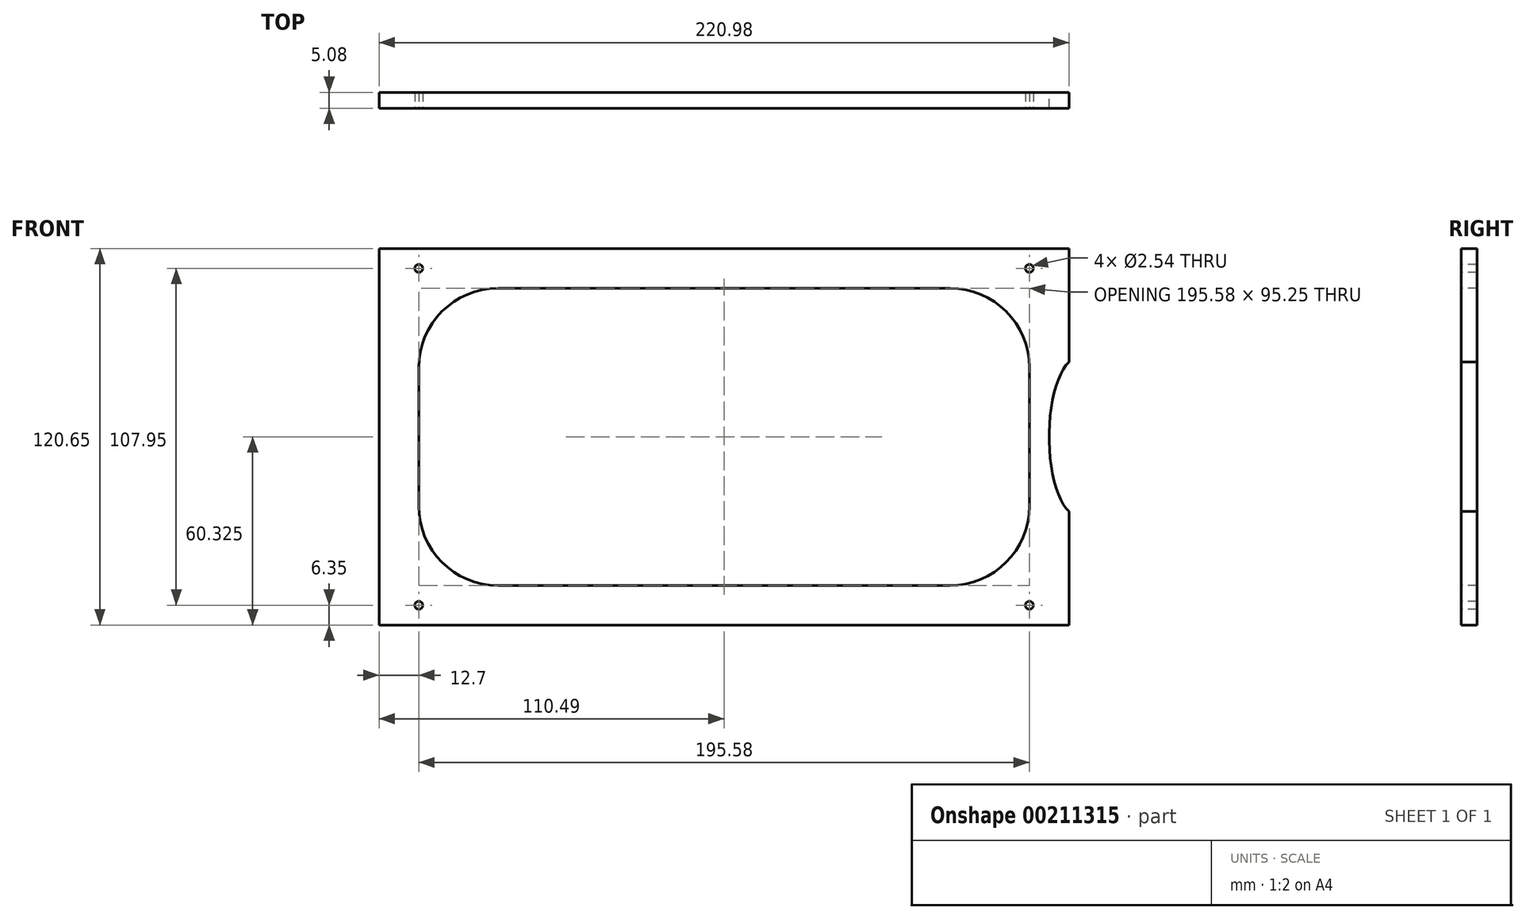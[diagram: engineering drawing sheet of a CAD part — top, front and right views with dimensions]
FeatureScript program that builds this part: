
annotation { "Feature Type Name" : "Feature", "Feature Type Description" : "" }
export const myFeature = defineFeature(function(context is Context, id is Id, definition is map)
    precondition{}
    {
        {
            var Q0;
            Q0=qCreatedBy(makeId("Front.planeOp"),FACE);
            var sketch = newSketch(context, id + "F0", { "sketchPlane" : qUnion([Q0])});
            skLineSegment(sketch, "E0.bottom", {"start": v(0, 0) * mm, "end": v(220.98, 0) * mm});
            skLineSegment(sketch, "E0.top", {"start": v(0, 120.65) * mm, "end": v(220.98, 120.65) * mm});
            skLineSegment(sketch, "E0.left", {"start": v(0, 0) * mm, "end": v(0, 120.65) * mm});
            skLineSegment(sketch, "E0.right", {"start": v(220.98, 0) * mm, "end": v(220.98, 120.65) * mm});
            skSolve(sketch);
        }
        {
            var Q0;
            Q0=makeQuery(id+"F0.imprint","IMPRINT",FACE,{"disambiguationData":[TD([[makeQuery(id+"F0.imprint","IMPRINT",EDGE,{"derivedFrom":sQuery(id+"F0.wireOp",EDGE,"E0.bottom")}),1.0]])]});
            extrude(context, id + "F1", {"entities" : qUnion([Q0]), "depth" : 5.08 * mm});
        }
        {
            var Q0;
            Q0=makeQuery(id+"F1.opExtrude","CAP_FACE",FACE,{"disambiguationData":[OSD([sQuery(id+"F0.wireOp",EDGE,"E0.bottom"),sQuery(id+"F0.wireOp",EDGE,"E0.top"),sQuery(id+"F0.wireOp",EDGE,"E0.left"),sQuery(id+"F0.wireOp",EDGE,"E0.right")])],"isStart":false});
            var sketch = newSketch(context, id + "F2", { "sketchPlane" : qUnion([Q0])});
            skLineSegment(sketch, "E1", {"start": v(12.7, 38.1) * mm, "end": v(12.7, 82.55) * mm});
            skLineSegment(sketch, "E2", {"start": v(38.1, 107.95) * mm, "end": v(182.88, 107.95) * mm});
            skLineSegment(sketch, "E3", {"start": v(208.28, 82.55) * mm, "end": v(208.28, 38.1) * mm});
            skLineSegment(sketch, "E4", {"start": v(182.88, 12.7) * mm, "end": v(38.1, 12.7) * mm});
            skPoint(sketch, "E5.visualSharp", {"position": v(12.7, 107.95) * mm});
            skArc(sketch, "E5.filletArc", {"start": v(38.1, 107.95) * mm, "mid": v(20.14, 100.51) * mm, "end": v(12.7, 82.55) * mm});
            skPoint(sketch, "E6.visualSharp", {"position": v(12.7, 12.7) * mm});
            skArc(sketch, "E6.filletArc", {"start": v(12.7, 38.1) * mm, "mid": v(20.14, 20.14) * mm, "end": v(38.1, 12.7) * mm});
            skPoint(sketch, "E7.visualSharp", {"position": v(208.28, 107.95) * mm});
            skArc(sketch, "E7.filletArc", {"start": v(208.28, 82.55) * mm, "mid": v(200.84, 100.51) * mm, "end": v(182.88, 107.95) * mm});
            skPoint(sketch, "E8.visualSharp", {"position": v(208.28, 12.7) * mm});
            skArc(sketch, "E8.filletArc", {"start": v(182.88, 12.7) * mm, "mid": v(200.84, 20.14) * mm, "end": v(208.28, 38.1) * mm});
            skSolve(sketch);
        }
        {
            var Q0;
            Q0=makeQuery(id+"F2.imprint","IMPRINT",FACE,{"disambiguationData":[TD([[makeQuery(id+"F2.imprint","IMPRINT",EDGE,{"derivedFrom":sQuery(id+"F2.wireOp",EDGE,"E1")}),-1.0]])]});
            extrude(context, id + "F3", {"entities" : qUnion([Q0]), "operationType" : NewBodyOperationType.REMOVE, "endBound" : BoundingType.THROUGH_ALL, "oppositeDirection" : true, "depth" : 25.4 * mm});
        }
        {
            var Q0;
            Q0=makeQuery(id+"F1.opExtrude","CAP_FACE",FACE,{"disambiguationData":[OSD([sQuery(id+"F0.wireOp",EDGE,"E0.bottom"),sQuery(id+"F0.wireOp",EDGE,"E0.top"),sQuery(id+"F0.wireOp",EDGE,"E0.left"),sQuery(id+"F0.wireOp",EDGE,"E0.right")])],"isStart":false});
            var sketch = newSketch(context, id + "F4", { "sketchPlane" : qUnion([Q0])});
            skCircle(sketch, "E9", {"center": v(12.7, 114.3) * mm, "radius": 1.27 * mm});
            skCircle(sketch, "E10", {"center": v(12.7, 6.35) * mm, "radius": 1.27 * mm});
            skCircle(sketch, "E11", {"center": v(208.28, 114.3) * mm, "radius": 1.27 * mm});
            skCircle(sketch, "E12", {"center": v(208.28, 6.35) * mm, "radius": 1.27 * mm});
            skEllipse(sketch, "E13", {"center": v(224.16, 60.32) * mm, "majorRadius": 25.4 * mm, "minorRadius": 9.53 * mm, "majorAxis": v(0, 1)});
            skSolve(sketch);
        }
        {
            var Q0;
            Q0 = qSketchRegion(id + "F4", true);
            extrude(context, id + "F5", {"entities" : qUnion([Q0]), "operationType" : NewBodyOperationType.REMOVE, "endBound" : BoundingType.THROUGH_ALL, "oppositeDirection" : true, "depth" : 25.4 * mm});
        }
    });
